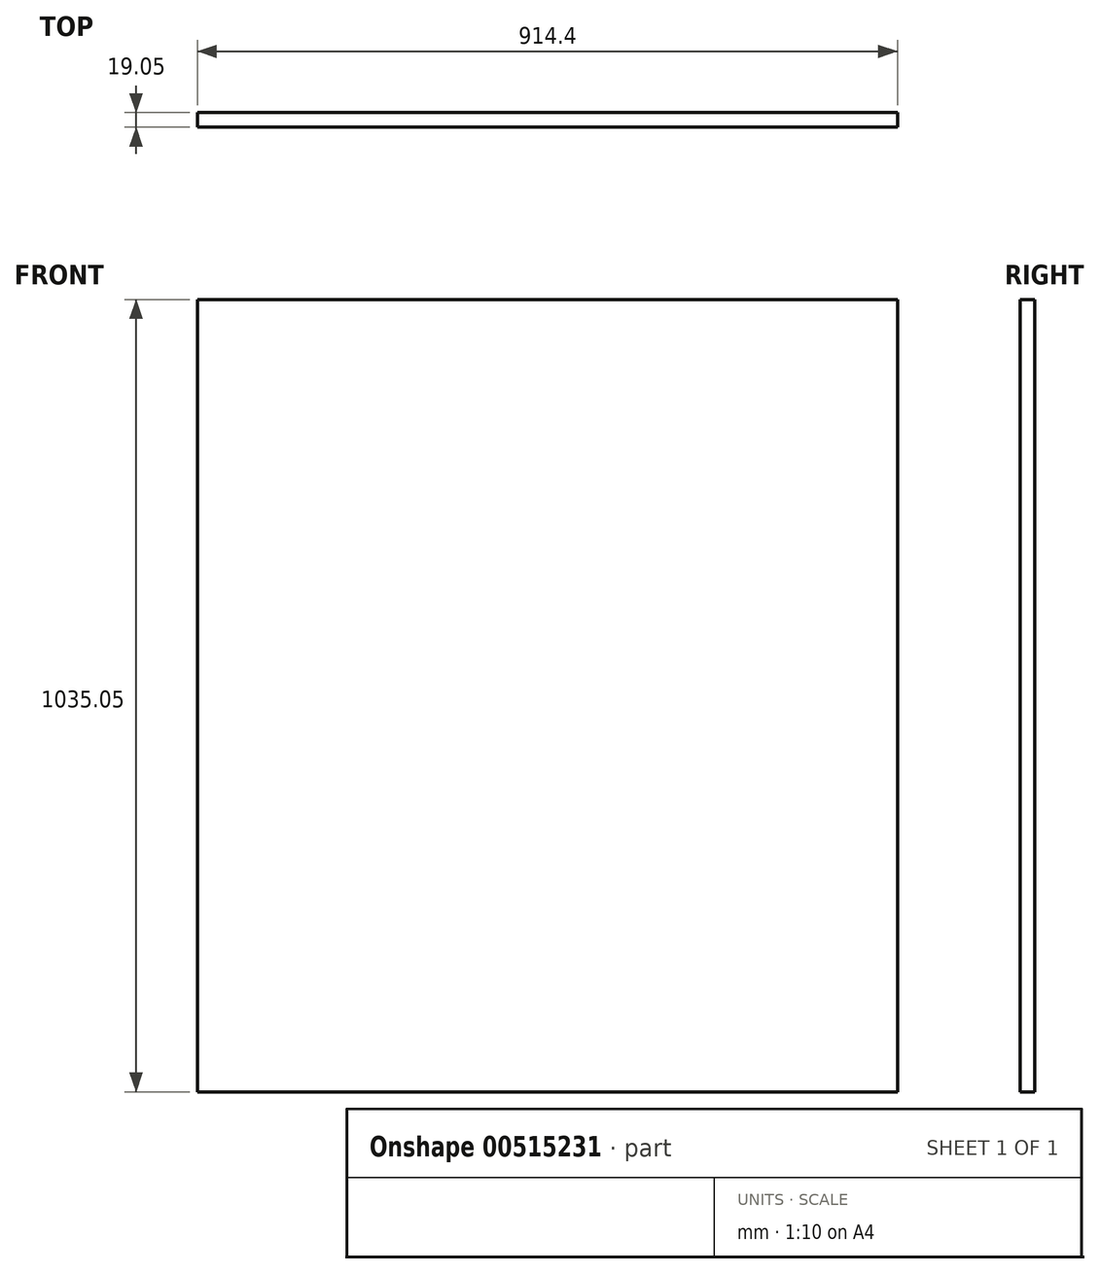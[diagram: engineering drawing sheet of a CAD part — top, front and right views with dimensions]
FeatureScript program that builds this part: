
annotation { "Feature Type Name" : "Feature", "Feature Type Description" : "" }
export const myFeature = defineFeature(function(context is Context, id is Id, definition is map)
    precondition{}
    {
        {
            var Q0;
            Q0=qCreatedBy(makeId("Top.planeOp"),FACE);
            var sketch = newSketch(context, id + "F0", { "sketchPlane" : qUnion([Q0])});
            skLineSegment(sketch, "E0.bottom", {"start": v(710.31, 0) * mm, "end": v(-204.09, 0) * mm});
            skLineSegment(sketch, "E0.top", {"start": v(710.31, 19.05) * mm, "end": v(-204.09, 19.05) * mm});
            skLineSegment(sketch, "E0.left", {"start": v(710.31, 0) * mm, "end": v(710.31, 19.05) * mm});
            skLineSegment(sketch, "E0.right", {"start": v(-204.09, 0) * mm, "end": v(-204.09, 19.05) * mm});
            skPoint(sketch, "E0.middle", {"position": v(253.11, 9.52) * mm});
            skSolve(sketch);
        }
        {
            var Q0;
            Q0=qSketchRegion(id+"F0",true);
            extrude(context, id + "F1", {"entities" : qUnion([Q0]), "depth" : 1035.05 * mm});
        }
    });
